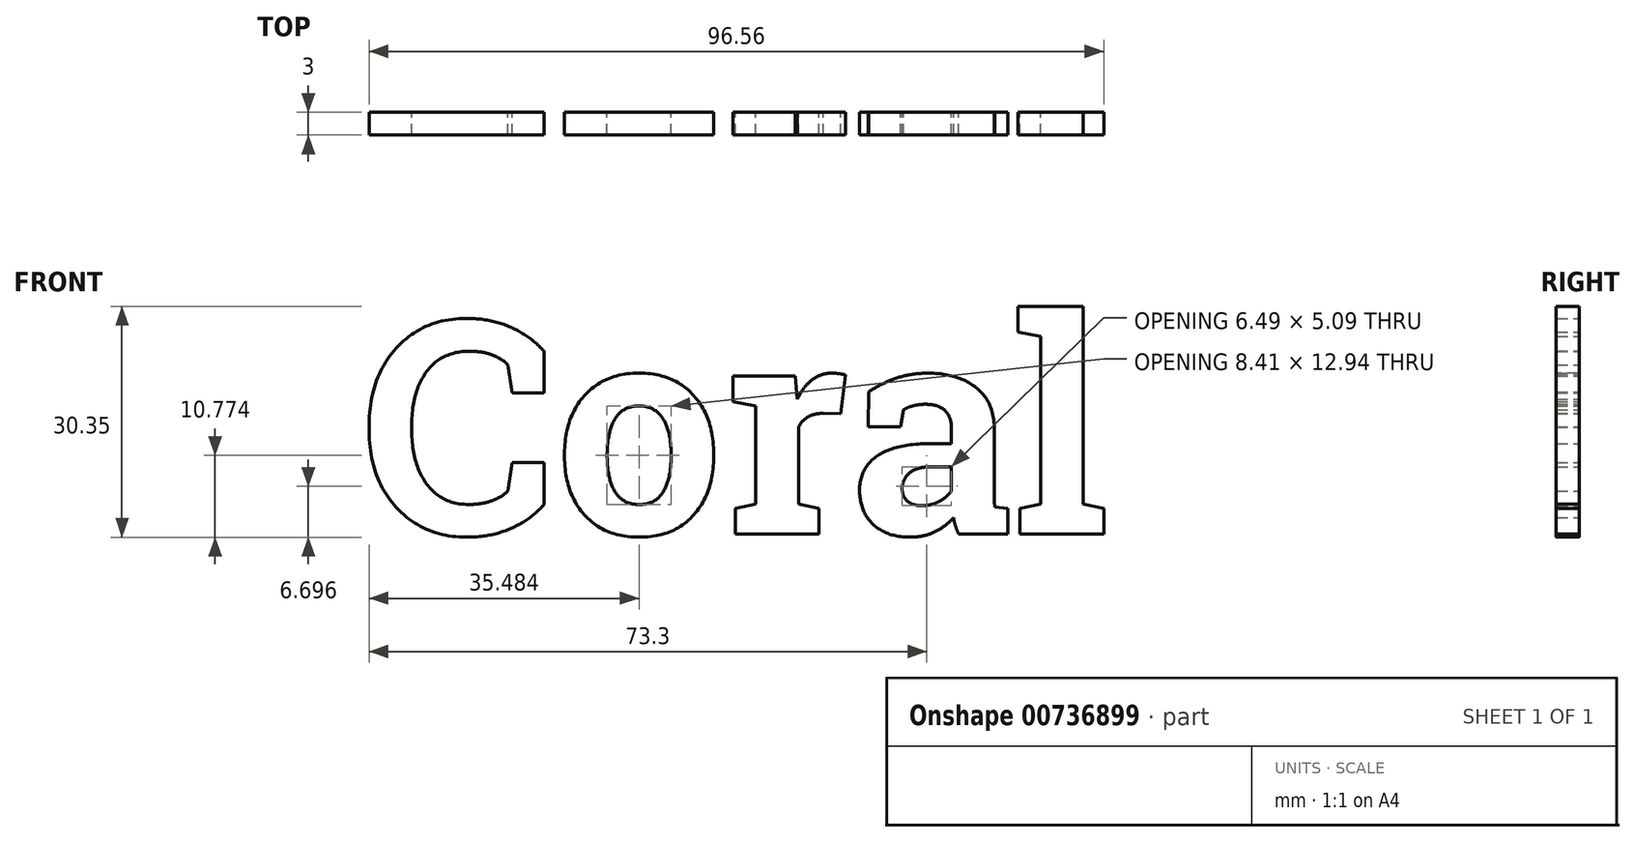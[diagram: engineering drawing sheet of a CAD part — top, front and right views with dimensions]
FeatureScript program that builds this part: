
annotation { "Feature Type Name" : "Feature", "Feature Type Description" : "" }
export const myFeature = defineFeature(function(context is Context, id is Id, definition is map)
    precondition{}
    {
        {
            var Q0;
            Q0=qCreatedBy(makeId("Front.planeOp"),FACE);
            var sketch = newSketch(context, id + "F0", { "sketchPlane" : qUnion([Q0])});
            skText(sketch, "E0", { "text": "Coral", "fontName": "RobotoSlab-Bold.ttf"});
            const initialGuessF0  = {"E0": [-0.05662, -0.01218, 1, 0, 0.0283]};
            skSetInitialGuess(sketch, initialGuessF0);
            skSolve(sketch);
        }
        {
            var Q0;
            Q0 = qSketchRegion(id + "F0", true);
            extrude(context, id + "F1", {"entities" : qUnion([Q0]), "depth" : 3 * mm, "offsetDistance" : 25 * mm});
        }
    });
